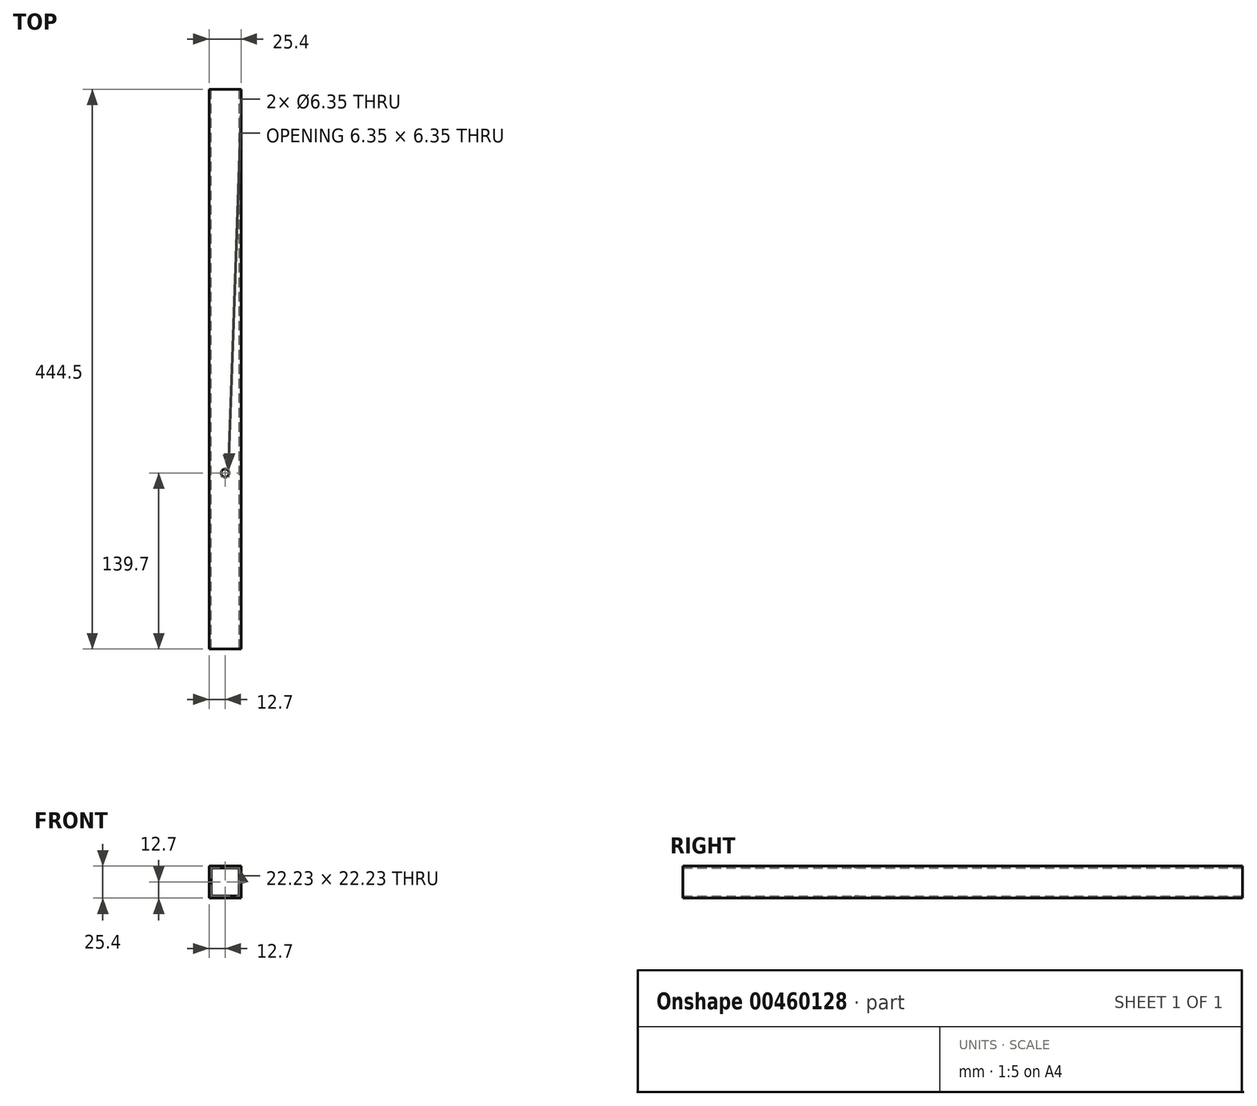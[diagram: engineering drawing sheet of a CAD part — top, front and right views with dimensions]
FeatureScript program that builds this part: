
annotation { "Feature Type Name" : "Feature", "Feature Type Description" : "" }
export const myFeature = defineFeature(function(context is Context, id is Id, definition is map)
    precondition{}
    {
        {
            var Q0;
            Q0=qCreatedBy(makeId("Front.planeOp"),FACE);
            var sketch = newSketch(context, id + "F0", { "sketchPlane" : qUnion([Q0])});
            skLineSegment(sketch, "E0.bottom", {"start": v(12.7, 12.7) * mm, "end": v(-12.7, 12.7) * mm});
            skLineSegment(sketch, "E0.top", {"start": v(12.7, -12.7) * mm, "end": v(-12.7, -12.7) * mm});
            skLineSegment(sketch, "E0.left", {"start": v(12.7, 12.7) * mm, "end": v(12.7, -12.7) * mm});
            skLineSegment(sketch, "E0.right", {"start": v(-12.7, 12.7) * mm, "end": v(-12.7, -12.7) * mm});
            skPoint(sketch, "E0.middle", {"position": v(0, 0) * mm});
            skLineSegment(sketch, "E1.bottom", {"start": v(11.11, 11.11) * mm, "end": v(-11.11, 11.11) * mm});
            skLineSegment(sketch, "E1.top", {"start": v(11.11, -11.11) * mm, "end": v(-11.11, -11.11) * mm});
            skLineSegment(sketch, "E1.left", {"start": v(11.11, 11.11) * mm, "end": v(11.11, -11.11) * mm});
            skLineSegment(sketch, "E1.right", {"start": v(-11.11, 11.11) * mm, "end": v(-11.11, -11.11) * mm});
            skSolve(sketch);
        }
        {
            var Q0;
            Q0=makeQuery(id+"F0.imprint","IMPRINT",FACE,{"disambiguationData":[TD([[makeQuery(id+"F0.imprint","IMPRINT",EDGE,{"derivedFrom":sQuery(id+"F0.wireOp",EDGE,"E0.bottom")}),1.0]])]});
            extrude(context, id + "F1", {"entities" : qUnion([Q0]), "depth" : 444.5 * mm});
        }
        {
            var Q0;
            Q0=makeQuery(id+"F1.opExtrude","SWEPT_FACE",FACE,{"disambiguationData":[OSD([sQuery(id+"F0.wireOp",EDGE,"E0.bottom")])]});
            var sketch = newSketch(context, id + "F2", { "sketchPlane" : qUnion([Q0])});
            skCircle(sketch, "E2", {"center": v(0, -304.8) * mm, "radius": 3.18 * mm});
            skSolve(sketch);
        }
        {
            var Q0;
            Q0=makeQuery(id+"F2.imprint","IMPRINT",FACE,{"disambiguationData":[TD([[makeQuery(id+"F2.imprint","IMPRINT",EDGE,{"derivedFrom":sQuery(id+"F2.wireOp",EDGE,"E2")}),1.0]])]});
            extrude(context, id + "F3", {"entities" : qUnion([Q0]), "operationType" : NewBodyOperationType.REMOVE, "oppositeDirection" : true, "depth" : 25.4 * mm});
        }
    });
